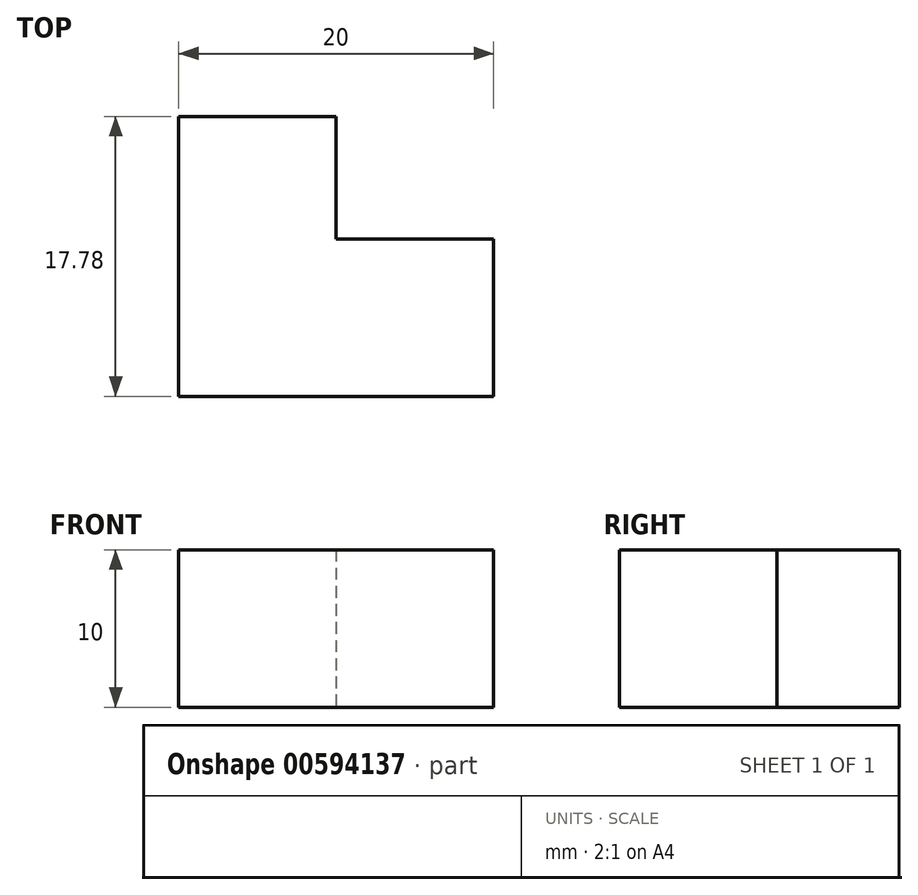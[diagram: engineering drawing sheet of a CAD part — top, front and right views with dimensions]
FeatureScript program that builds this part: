
annotation { "Feature Type Name" : "Feature", "Feature Type Description" : "" }
export const myFeature = defineFeature(function(context is Context, id is Id, definition is map)
    precondition{}
    {
        {
            var Q0;
            Q0=qCreatedBy(makeId("Top.planeOp"),FACE);
            var sketch = newSketch(context, id + "F0", { "sketchPlane" : qUnion([Q0])});
            skLineSegment(sketch, "E0", {"start": v(0, 0) * mm, "end": v(0, 20) * mm});
            skLineSegment(sketch, "E1", {"start": v(0, 17.78) * mm, "end": v(10, 17.78) * mm});
            skLineSegment(sketch, "E2", {"start": v(10, 17.78) * mm, "end": v(10, 10) * mm});
            skLineSegment(sketch, "E3", {"start": v(10, 10) * mm, "end": v(20, 10) * mm});
            skLineSegment(sketch, "E4", {"start": v(20, 10) * mm, "end": v(20, 0) * mm});
            skLineSegment(sketch, "E5", {"start": v(20, 0) * mm, "end": v(0, 0) * mm});
            skSolve(sketch);
        }
        {
            var Q0;
            {var subQ0=sQuery(id+"F0.wireOp",EDGE,"E1");Q0=makeQuery(id+"F0.imprint","IMPRINT",FACE,{"disambiguationData":[TD([[makeQuery(id+"F0.imprint","IMPRINT",EDGE,{"derivedFrom":subQ0}),-1.0]])]});}
            extrude(context, id + "F1", {"entities" : qUnion([Q0]), "depth" : 10 * mm, "offsetDistance" : 25 * mm});
        }
    });
